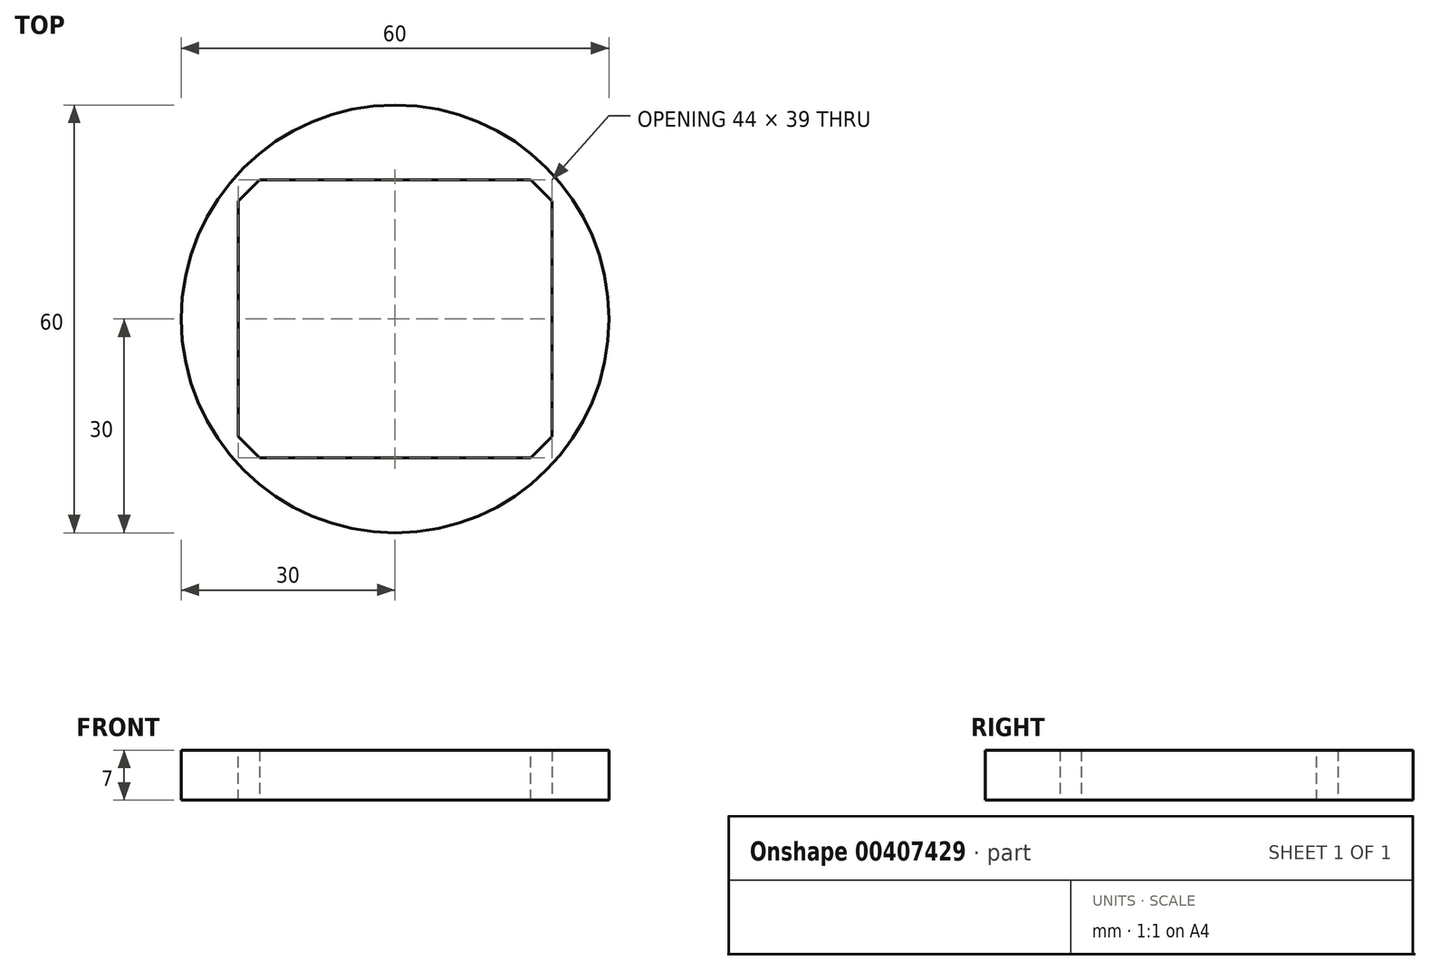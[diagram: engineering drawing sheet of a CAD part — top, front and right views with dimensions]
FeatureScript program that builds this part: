
annotation { "Feature Type Name" : "Feature", "Feature Type Description" : "" }
export const myFeature = defineFeature(function(context is Context, id is Id, definition is map)
    precondition{}
    {
        {
            var Q0;
            Q0=qCreatedBy(makeId("Top.planeOp"),FACE);
            var sketch = newSketch(context, id + "F0", { "sketchPlane" : qUnion([Q0])});
            skLineSegment(sketch, "E0.bottom", {"start": v(-22, 19.5) * mm, "end": v(22, 19.5) * mm});
            skLineSegment(sketch, "E0.top", {"start": v(-22, -19.5) * mm, "end": v(22, -19.5) * mm});
            skLineSegment(sketch, "E0.left", {"start": v(-22, 19.5) * mm, "end": v(-22, -19.5) * mm});
            skLineSegment(sketch, "E0.right", {"start": v(22, 19.5) * mm, "end": v(22, -19.5) * mm});
            skPoint(sketch, "E0.middle", {"position": v(0, 0) * mm});
            skCircle(sketch, "E1", {"center": v(0, 0) * mm, "radius": 30 * mm});
            skSolve(sketch);
        }
        {
            var Q0;
            Q0=makeQuery(id+"F0.imprint","IMPRINT",FACE,{"disambiguationData":[TD([[makeQuery(id+"F0.imprint","IMPRINT",EDGE,{"derivedFrom":sQuery(id+"F0.wireOp",EDGE,"E0.bottom")}),1.0]])]});
            extrude(context, id + "F1", {"entities" : qUnion([Q0]), "depth" : 7 * mm});
        }
        {
            var Q0;
            Q0=makeQuery(id+"F1.opExtrude","SWEPT_EDGE",EDGE,{"disambiguationData":[OSD([sQuery(id+"F0.wireOp",EDGE,"E0.bottom"),sQuery(id+"F0.wireOp",EDGE,"E0.left")])]});
            var Q1;
            Q1=makeQuery(id+"F1.opExtrude","SWEPT_EDGE",EDGE,{"disambiguationData":[OSD([sQuery(id+"F0.wireOp",EDGE,"E0.bottom"),sQuery(id+"F0.wireOp",EDGE,"E0.right")])]});
            var Q2;
            Q2=makeQuery(id+"F1.opExtrude","SWEPT_EDGE",EDGE,{"disambiguationData":[OSD([sQuery(id+"F0.wireOp",EDGE,"E0.top"),sQuery(id+"F0.wireOp",EDGE,"E0.left")])]});
            var Q3;
            Q3=makeQuery(id+"F1.opExtrude","SWEPT_EDGE",EDGE,{"disambiguationData":[OSD([sQuery(id+"F0.wireOp",EDGE,"E0.top"),sQuery(id+"F0.wireOp",EDGE,"E0.right")])]});
            chamfer(context, id + "F2", {"entities" : qUnion([Q0, Q1, Q2, Q3]), "width" : 3 * mm, "tangentPropagation" : true});
        }
    });
